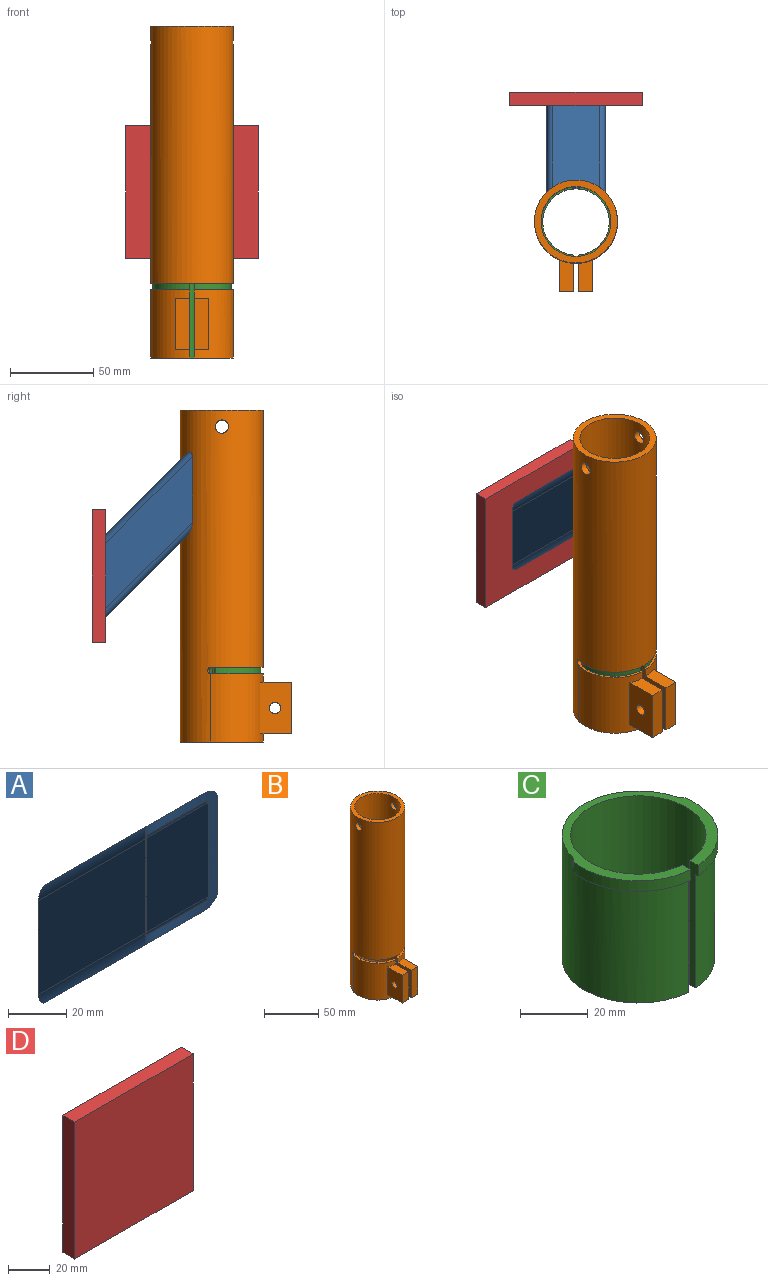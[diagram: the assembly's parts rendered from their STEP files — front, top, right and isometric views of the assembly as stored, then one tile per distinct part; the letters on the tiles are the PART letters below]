
ASSEMBLY  parts=4 mates=3
PART A: 18 faces, bbox 35x57.1x100 mm
  f0: plane 49.29x49.29mm, normal (0,0.71,0.71), area 1836.4mm2, adj f2,f6,f8,f17
  f1: plane 49.29x49.29mm, normal (0,-0.71,-0.71), area 1836.4mm2, adj f2,f5,f7,f17
  f2: plane 49.5x35mm, normal (0,1,0), area 446mm2, adj f0,f1,f3,f4,f5,f6,f7,f8
  f3: plane 91.74x52.15mm, normal (1,0,0), area 2064.9mm2, adj f2,f7,f8,f17
  f4: plane 91.74x52.15mm, normal (-1,0,0), area 2064.9mm2, adj f2,f5,f6,f17
  f5: cylinder r=3.5mm len=57.1mm, axis (0,0.71,-0.71), area 396.8mm2, adj f1,f2,f4,f17
  f6: cylinder r=3.5mm len=55.45mm, axis (0,-0.71,0.71), area 396.8mm2, adj f0,f2,f4,f17
  f7: cylinder r=3.5mm len=57.1mm, axis (0,-0.71,0.71), area 396.8mm2, adj f1,f2,f3,f17
  f8: cylinder r=3.5mm len=55.45mm, axis (0,0.71,-0.71), area 396.8mm2, adj f0,f2,f3,f17
  f9: plane 49.29x49.29mm, normal (0,-0.71,-0.71), area 1836.4mm2, adj f2,f14,f16,f17
  f10: plane 49.29x49.29mm, normal (0,0.71,0.71), area 1836.4mm2, adj f2,f13,f15,f17
  f11: plane 89.6x50mm, normal (-1,0,0), area 1979.9mm2, adj f2,f15,f16,f17
  f12: plane 89.6x50mm, normal (1,0,0), area 1979.9mm2, adj f2,f13,f14,f17
  f13: cylinder r=1mm len=51.41mm, axis (0,0.71,-0.71), area 110.5mm2, adj f2,f10,f12,f17
  f14: cylinder r=1mm len=50.99mm, axis (0,-0.71,0.71), area 110.5mm2, adj f2,f9,f12,f17
  f15: cylinder r=1mm len=51.41mm, axis (0,-0.71,0.71), area 110.5mm2, adj f2,f10,f11,f17
  f16: cylinder r=1mm len=50.99mm, axis (0,0.71,-0.71), area 110.5mm2, adj f2,f9,f11,f17
  f17: cylinder r=25mm len=54.43mm, axis (0,0,1), area 535.4mm2, adj f0,f1,f3,f4,f5,f6,f7,f8
PART B: 25 faces, bbox 50x67x200 mm
  f0: cylinder r=21mm len=155mm, axis (0,0,-1), area 20350.8mm2, adj f6,f8,f9,f15
  f1: cylinder r=25mm len=200mm, axis (0,0,-1), area 28714.1mm2, adj f2,f3,f5,f6,f7,f8,f9,f13
  f2: cylinder r=25mm len=41mm, axis (0,0,-1), area 1551.8mm2, adj f1,f7,f10,f12,f14,f16,f19
  f3: plane 19.09x8.5mm, normal (0,0,-1), area 151.3mm2, adj f1,f4,f13,f17
  f4: plane 31x8.5mm, normal (0,-1,0), area 263.5mm2, adj f3,f5,f13,f17
  f5: plane 19.09x8.5mm, normal (0,0,1), area 151.3mm2, adj f1,f4,f13,f17
  f6: plane 50x50mm, normal (0,0,1), area 578.1mm2, adj f0,f1
  f7: plane 50x49.96mm, normal (0,0,-1), area 365.6mm2, adj f1,f2,f16,f17,f22
  f8: cylinder r=4mm len=8mm, axis (1,0,0), area 101.3mm2, adj f0,f1
  f9: cylinder r=4mm len=8mm, axis (1,0,0), area 101.3mm2, adj f0,f1
  f10: plane 19.09x8.5mm, normal (0,0,-1), area 151.3mm2, adj f2,f11,f12,f16
  f11: plane 31x8.5mm, normal (0,-1,0), area 263.5mm2, adj f10,f12,f14,f16
  f12: plane 31x19.09mm, normal (-1,0,0), area 555.4mm2, adj f2,f10,f11,f14,f24
  f13: plane 31x19.09mm, normal (1,0,0), area 528.1mm2, adj f1,f3,f4,f5,f23
  f14: plane 19.09x8.5mm, normal (0,0,1), area 151.3mm2, adj f2,f11,f12,f16
  f15: plane 50x47.5mm, normal (0,0,-1), area 423mm2, adj f0,f1,f20,f21,f22
  f16: plane 41x19.55mm, normal (1,0,0), area 594.8mm2, adj f2,f7,f10,f11,f14,f19,f22,f24
  f17: plane 41x19.55mm, normal (-1,0,0), area 567.5mm2, adj f1,f3,f4,f5,f7,f18,f22,f23
  f18: plane 31.6x23.5mm, normal (0,0,1), area 105.2mm2, adj f1,f17,f21,f22
  f19: plane 31.6x23.5mm, normal (0,0,1), area 105.2mm2, adj f2,f16,f20,f22
  f20: cylinder r=2mm len=4mm, axis (-0.94,0.34,0), area 15.7mm2, adj f1,f15,f19,f22
  f21: cylinder r=2mm len=4mm, axis (-0.94,-0.34,0), area 15.7mm2, adj f1,f15,f18,f22
  f22: cylinder r=22.5mm len=45mm, axis (0,0,-1), area 5896.5mm2, adj f7,f15,f16,f17,f18,f19,f20,f21
  f23: cylinder r=4.5mm len=9mm, axis (1,0,0), area 240.3mm2, adj f13,f17
  f24: cylinder r=3.4mm len=8.5mm, axis (1,0,0), area 181.6mm2, adj f12,f16
PART C: 12 faces, bbox 47x46x44.8 mm
  f0: plane 29.36x22mm, normal (0,0,-1), area 39.3mm2, adj f1,f7,f9,f10
  f1: cylinder r=23.5mm len=27.53mm, axis (0,0,1), area 150.2mm2, adj f0,f5,f9,f10
  f2: plane 45x44.95mm, normal (0,0,-1), area 326.3mm2, adj f6,f7,f10,f11
  f3: plane 29.36x22mm, normal (0,0,-1), area 39.3mm2, adj f4,f7,f8,f11
  f4: cylinder r=23.5mm len=27.53mm, axis (0,0,1), area 150.2mm2, adj f3,f5,f8,f11
  f5: plane 47x45.95mm, normal (0,0,1), area 404.8mm2, adj f1,f4,f6,f7,f8,f9,f10,f11
  f6: cylinder r=20mm len=44.8mm, axis (0,0,1), area 5495.2mm2, adj f2,f5,f10,f11
  f7: cylinder r=22.5mm len=45mm, axis (0,0,1), area 5896.3mm2, adj f0,f2,f3,f5,f8,f9,f10,f11
  f8: cylinder r=3mm len=3.8mm, axis (0,0,1), area 9.1mm2, adj f3,f4,f5,f7
  f9: cylinder r=3mm len=3.8mm, axis (0,0,1), area 9.1mm2, adj f0,f1,f5,f7
  f10: plane 44.8x3.51mm, normal (-1,0,0), area 116.1mm2, adj f0,f1,f2,f5,f6,f7
  f11: plane 44.8x3.51mm, normal (1,0,0), area 116.1mm2, adj f2,f3,f4,f5,f6,f7
PART D: 6 faces, bbox 80x8x80 mm
  f0: plane 80x8mm, normal (0,0,1), area 640mm2, adj f1,f3,f4,f5
  f1: plane 80x8mm, normal (1,0,0), area 640mm2, adj f0,f2,f4,f5
  f2: plane 80x8mm, normal (0,0,-1), area 640mm2, adj f1,f3,f4,f5
  f3: plane 80x8mm, normal (-1,0,0), area 640mm2, adj f0,f2,f4,f5
  f4: plane 80x80mm, normal (0,1,0), area 6400mm2, adj f0,f1,f2,f3
  f5: plane 80x80mm, normal (0,-1,0), area 6400mm2, adj f0,f1,f2,f3
PLACE A t=(2.96,-2.29,150)mm
PLACE B t=(2.96,-2.29,150)mm
PLACE C t=(2.96,-2.29,150)mm
PLACE D t=(2.96,-2.29,150)mm
MATE fastened C.f1 <-> B.f1  axis (0,0,-1) through (2.96,-2.29,280)mm
MATE fastened D.f5 <-> A.f2  axis (0,-1,0) through (2.96,67.71,380)mm
MATE fastened A.f17 <-> B.f1  axis (0,0,1) through (2.96,-2.29,480)mm
